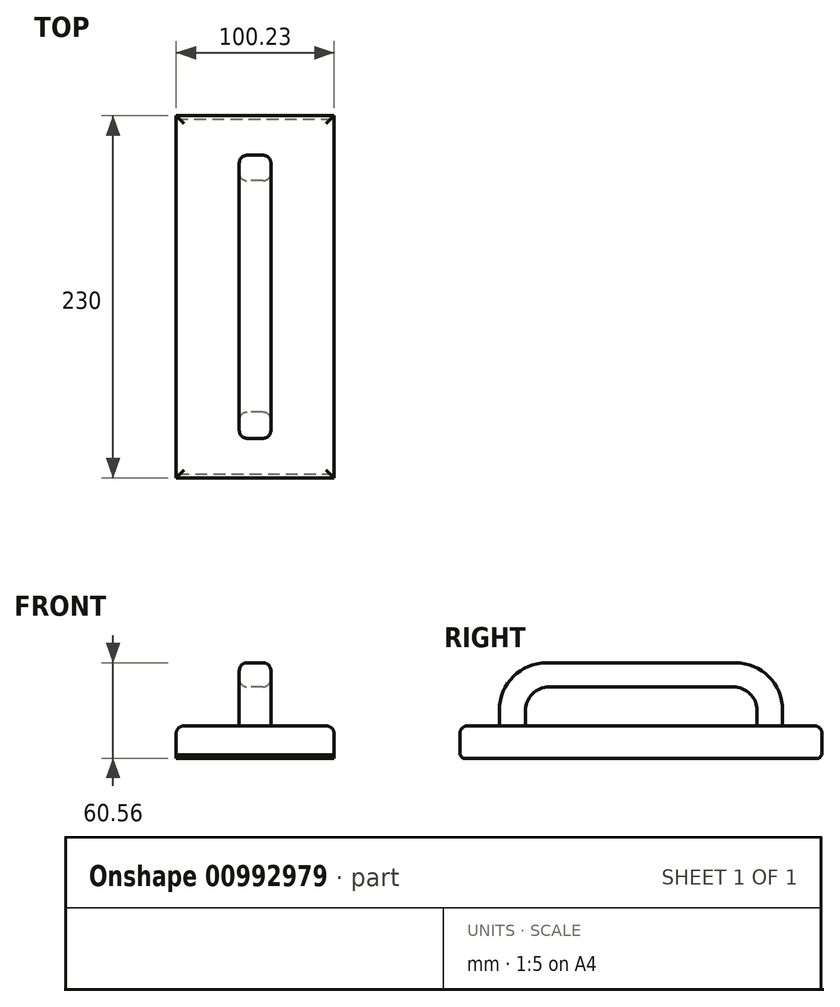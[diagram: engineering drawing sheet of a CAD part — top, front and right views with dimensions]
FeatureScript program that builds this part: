
annotation { "Feature Type Name" : "Feature", "Feature Type Description" : "" }
export const myFeature = defineFeature(function(context is Context, id is Id, definition is map)
    precondition{}
    {
        {
            var Q0;
            Q0=qCreatedBy(makeId("Front.planeOp"),FACE);
            var sketch = newSketch(context, id + "F0", { "sketchPlane" : qUnion([Q0])});
            skLineSegment(sketch, "E0.bottom", {"start": v(0, 0) * mm, "end": v(-100.23, 0) * mm});
            skLineSegment(sketch, "E0.top", {"start": v(0, 20.56) * mm, "end": v(-100.23, 20.56) * mm});
            skLineSegment(sketch, "E0.left", {"start": v(0, 0) * mm, "end": v(0, 20.56) * mm});
            skLineSegment(sketch, "E0.right", {"start": v(-100.23, 0) * mm, "end": v(-100.23, 20.56) * mm});
            skSolve(sketch);
        }
        {
            var Q0;
            Q0 = qSketchRegion(id + "F0", true);
            extrude(context, id + "F1", {"entities" : qUnion([Q0]), "depth" : 230 * mm, "offsetDistance" : 25 * mm});
        }
        {
            var Q0;
            Q0=makeQuery(id+"F1.opExtrude","CAP_EDGE",EDGE,{"disambiguationData":[OSD([sQuery(id+"F0.wireOp",EDGE,"E0.top")])],"isStart":false});
            var Q1;
            Q1=makeQuery(id+"F1.opExtrude","SWEPT_EDGE",EDGE,{"disambiguationData":[OSD([sQuery(id+"F0.wireOp",EDGE,"E0.top"),sQuery(id+"F0.wireOp",EDGE,"E0.left")])]});
            var Q2;
            Q2=makeQuery(id+"F1.opExtrude","SWEPT_EDGE",EDGE,{"disambiguationData":[OSD([sQuery(id+"F0.wireOp",EDGE,"E0.top"),sQuery(id+"F0.wireOp",EDGE,"E0.right")])]});
            var Q3;
            Q3=makeQuery(id+"F1.opExtrude","CAP_EDGE",EDGE,{"disambiguationData":[OSD([sQuery(id+"F0.wireOp",EDGE,"E0.top")])],"isStart":true});
            fillet(context, id + "F2", {"entities" : qUnion([Q0, Q1, Q2, Q3]), "radius" : 5 * mm, "tangentPropagation" : true, "allowEdgeOverflow" : false});
        }
        {
            var Q0;
            Q0=makeQuery(id+"F1.opExtrude","SWEPT_FACE",FACE,{"disambiguationData":[OSD([sQuery(id+"F0.wireOp",EDGE,"E0.top")])]});
            var sketch = newSketch(context, id + "F3", { "sketchPlane" : qUnion([Q0])});
            skLineSegment(sketch, "E1.bottom", {"start": v(-60.13, -25.11) * mm, "end": v(-40.1, -25.11) * mm});
            skLineSegment(sketch, "E1.top", {"start": v(-60.13, -204.89) * mm, "end": v(-40.1, -204.89) * mm});
            skLineSegment(sketch, "E1.left", {"start": v(-60.13, -25.11) * mm, "end": v(-60.13, -204.89) * mm});
            skLineSegment(sketch, "E1.right", {"start": v(-40.1, -25.11) * mm, "end": v(-40.1, -204.89) * mm});
            skPoint(sketch, "E1.middle", {"position": v(-50.11, -115) * mm});
            skPoint(sketch, "E1.middle.positionSnap0", {"position": v(-5, -115) * mm});
            skPoint(sketch, "E1.middle.positionSnap1", {"position": v(-50.11, -5) * mm});
            skPoint(sketch, "E1.centerSnap0", {"position": v(-5, -115) * mm});
            skPoint(sketch, "E1.centerSnap1", {"position": v(-50.11, -5) * mm});
            skSolve(sketch);
        }
        {
            var Q0;
            Q0 = qSketchRegion(id + "F3", true);
            extrude(context, id + "F4", {"entities" : qUnion([Q0]), "operationType" : NewBodyOperationType.ADD, "depth" : 40 * mm, "offsetDistance" : 25 * mm});
        }
        {
            var Q0;
            Q0=makeQuery(id+"F4.opExtrude","CAP_EDGE",EDGE,{"disambiguationData":[OSD([sQuery(id+"F3.wireOp",EDGE,"E1.bottom")])],"isStart":false});
            var Q1;
            Q1=makeQuery(id+"F4.opExtrude","CAP_EDGE",EDGE,{"disambiguationData":[OSD([sQuery(id+"F3.wireOp",EDGE,"E1.top")])],"isStart":false});
            fillet(context, id + "F5", {"entities" : qUnion([Q0, Q1]), "tangentPropagation" : true, "radius" : 30 * mm, "defaultsChanged" : true, "vertexSettings" : [], "allowEdgeOverflow" : false});
        }
        {
            var Q0;
            Q0=makeQuery(id+"F4.opExtrude","SWEPT_FACE",FACE,{"disambiguationData":[OSD([sQuery(id+"F3.wireOp",EDGE,"E1.left")])]});
            var sketch = newSketch(context, id + "F6", { "sketchPlane" : qUnion([Q0])});
            skLineSegment(sketch, "E2.bottom", {"start": v(41.3, 20.56) * mm, "end": v(188.33, 20.56) * mm});
            skLineSegment(sketch, "E2.top", {"start": v(41.3, 45.3) * mm, "end": v(188.33, 45.3) * mm});
            skLineSegment(sketch, "E2.left", {"start": v(41.3, 20.56) * mm, "end": v(41.3, 45.3) * mm});
            skLineSegment(sketch, "E2.right", {"start": v(188.33, 20.56) * mm, "end": v(188.33, 45.3) * mm});
            skSolve(sketch);
        }
        {
            var Q0;
            Q0=makeQuery(id+"F6.imprint","IMPRINT",FACE,{"disambiguationData":[TD([[makeQuery(id+"F6.imprint","IMPRINT",EDGE,{"derivedFrom":sQuery(id+"F6.wireOp",EDGE,"E2.bottom")}),1.0]])]});
            extrude(context, id + "F7", {"entities" : qUnion([Q0]), "operationType" : NewBodyOperationType.REMOVE, "oppositeDirection" : true, "depth" : 25 * mm, "offsetDistance" : 25 * mm});
        }
        {
            var Q0;
            Q0=makeQuery(id+"F7.boolean.opBoolean","COPY",EDGE,{"derivedFrom":makeQuery(id+"F7.opExtrude","SWEPT_EDGE",EDGE,{"disambiguationData":[OSD([sQuery(id+"F6.wireOp",EDGE,"E2.top"),sQuery(id+"F6.wireOp",EDGE,"E2.right")])]})});
            var Q1;
            Q1=makeQuery(id+"F7.boolean.opBoolean","COPY",EDGE,{"derivedFrom":makeQuery(id+"F7.opExtrude","SWEPT_EDGE",EDGE,{"disambiguationData":[OSD([sQuery(id+"F6.wireOp",EDGE,"E2.top"),sQuery(id+"F6.wireOp",EDGE,"E2.left")])]})});
            fillet(context, id + "F8", {"entities" : qUnion([Q0, Q1]), "tangentPropagation" : true, "radius" : 15 * mm, "defaultsChanged" : false, "vertexSettings" : [], "allowEdgeOverflow" : false});
        }
        {
            var Q0;
            Q0=makeQuery(id+"F4.opExtrude","CAP_EDGE",EDGE,{"disambiguationData":[OSD([sQuery(id+"F3.wireOp",EDGE,"E1.left")])],"isStart":false});
            var Q1;
            Q1=makeQuery(id+"F5.opFillet","BLEND_EDGE",EDGE,{"blendedFrom":[makeQuery(id+"F4.opExtrude","CAP_EDGE",EDGE,{"disambiguationData":[OSD([sQuery(id+"F3.wireOp",EDGE,"E1.bottom")])],"isStart":false}),makeQuery(id+"F4.opExtrude","SWEPT_FACE",FACE,{"disambiguationData":[OSD([sQuery(id+"F3.wireOp",EDGE,"E1.left")])]})],"blendedInto":[makeQuery(id+"F4.opExtrude","SWEPT_FACE",FACE,{"disambiguationData":[OSD([sQuery(id+"F3.wireOp",EDGE,"E1.left")])]})]});
            var Q2;
            Q2=makeQuery(id+"F7.boolean.opBoolean","COPY",EDGE,{"derivedFrom":makeQuery(id+"F7.opExtrude","CAP_EDGE",EDGE,{"disambiguationData":[OSD([sQuery(id+"F6.wireOp",EDGE,"E2.top")])],"isStart":true})});
            var Q3;
            Q3=makeQuery(id+"F8.opFillet","BLEND_EDGE",EDGE,{"blendedFrom":[makeQuery(id+"F7.boolean.opBoolean","COPY",EDGE,{"derivedFrom":makeQuery(id+"F7.opExtrude","SWEPT_EDGE",EDGE,{"disambiguationData":[OSD([sQuery(id+"F6.wireOp",EDGE,"E2.top"),sQuery(id+"F6.wireOp",EDGE,"E2.left")])]})}),makeQuery(id+"F4.opExtrude","SWEPT_FACE",FACE,{"disambiguationData":[OSD([sQuery(id+"F3.wireOp",EDGE,"E1.left")])]})],"blendedInto":[makeQuery(id+"F4.opExtrude","SWEPT_FACE",FACE,{"disambiguationData":[OSD([sQuery(id+"F3.wireOp",EDGE,"E1.left")])]})]});
            var Q4;
            Q4=makeQuery(id+"F8.opFillet","BLEND_EDGE",EDGE,{"blendedFrom":[makeQuery(id+"F7.boolean.opBoolean","COPY",EDGE,{"derivedFrom":makeQuery(id+"F7.opExtrude","SWEPT_EDGE",EDGE,{"disambiguationData":[OSD([sQuery(id+"F6.wireOp",EDGE,"E2.top"),sQuery(id+"F6.wireOp",EDGE,"E2.right")])]})}),makeQuery(id+"F4.opExtrude","SWEPT_FACE",FACE,{"disambiguationData":[OSD([sQuery(id+"F3.wireOp",EDGE,"E1.left")])]})],"blendedInto":[makeQuery(id+"F4.opExtrude","SWEPT_FACE",FACE,{"disambiguationData":[OSD([sQuery(id+"F3.wireOp",EDGE,"E1.left")])]})]});
            var Q5;
            Q5=makeQuery(id+"F4.opExtrude","CAP_EDGE",EDGE,{"disambiguationData":[OSD([sQuery(id+"F3.wireOp",EDGE,"E1.right")])],"isStart":false});
            var Q6;
            Q6=makeQuery(id+"F5.opFillet","BLEND_EDGE",EDGE,{"blendedFrom":[makeQuery(id+"F4.opExtrude","CAP_EDGE",EDGE,{"disambiguationData":[OSD([sQuery(id+"F3.wireOp",EDGE,"E1.top")])],"isStart":false}),makeQuery(id+"F4.opExtrude","SWEPT_FACE",FACE,{"disambiguationData":[OSD([sQuery(id+"F3.wireOp",EDGE,"E1.right")])]})],"blendedInto":[makeQuery(id+"F4.opExtrude","SWEPT_FACE",FACE,{"disambiguationData":[OSD([sQuery(id+"F3.wireOp",EDGE,"E1.right")])]})]});
            var Q7;
            Q7=makeQuery(id+"F7.boolean.opBoolean","INTERSECT",EDGE,{"derivedFrom":[makeQuery(id+"F4.opExtrude","SWEPT_FACE",FACE,{"disambiguationData":[OSD([sQuery(id+"F3.wireOp",EDGE,"E1.right")])]}),makeQuery(id+"F7.opExtrude","SWEPT_FACE",FACE,{"disambiguationData":[OSD([sQuery(id+"F6.wireOp",EDGE,"E2.top")])]})]});
            fillet(context, id + "F9", {"entities" : qUnion([Q0, Q1, Q2, Q3, Q4, Q5, Q6, Q7]), "tangentPropagation" : true, "radius" : 5 * mm, "defaultsChanged" : false, "vertexSettings" : [], "allowEdgeOverflow" : false});
        }
        {
            var Q0;
            Q0=makeQuery(id+"F1.opExtrude","CAP_EDGE",EDGE,{"disambiguationData":[OSD([sQuery(id+"F0.wireOp",EDGE,"E0.bottom")])],"isStart":false});
            chamfer(context, id + "F10", {"entities" : qUnion([Q0]), "width" : 2 * mm, "tangentPropagation" : true});
        }
        {
            var Q0;
            Q0=makeQuery(id+"F1.opExtrude","CAP_EDGE",EDGE,{"disambiguationData":[OSD([sQuery(id+"F0.wireOp",EDGE,"E0.bottom")])],"isStart":true});
            chamfer(context, id + "F11", {"entities" : qUnion([Q0]), "width" : 2 * mm, "tangentPropagation" : true});
        }
    });
